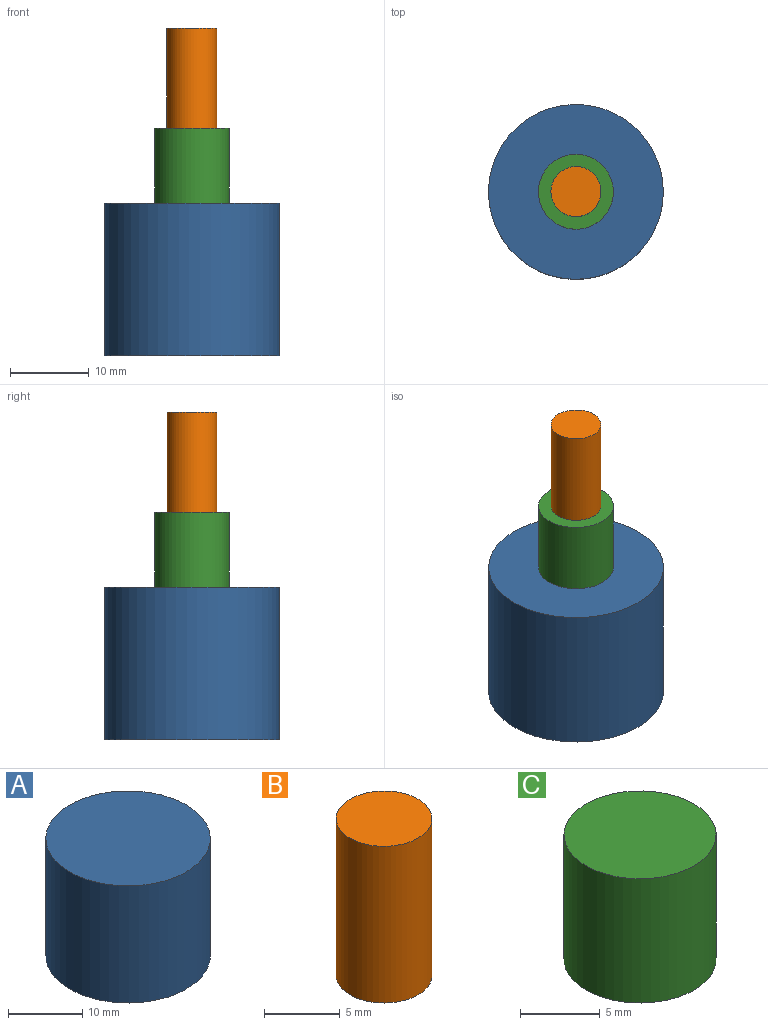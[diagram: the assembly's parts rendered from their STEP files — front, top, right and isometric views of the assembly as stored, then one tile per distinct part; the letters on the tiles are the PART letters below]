
ASSEMBLY  parts=3 mates=2
PART A: 3 faces, bbox 22.2x22.2x19.4 mm
  f0: cylinder r=11.11mm len=22.23mm, axis (0,0,-1), area 1353.2mm2, adj f1,f2
  f1: plane 22.23x22.23mm, normal (0,0,1), area 387.9mm2, adj f0
  f2: plane 22.23x22.23mm, normal (0,0,-1), area 387.9mm2, adj f0
PART B: 3 faces, bbox 6.4x6.4x12.7 mm
  f0: cylinder r=3.17mm len=12.7mm, axis (0,0,-1), area 253.4mm2, adj f1,f2
  f1: plane 6.35x6.35mm, normal (0,0,1), area 31.7mm2, adj f0
  f2: plane 6.35x6.35mm, normal (0,0,-1), area 31.7mm2, adj f0
PART C: 3 faces, bbox 9.5x9.5x9.5 mm
  f0: cylinder r=4.76mm len=9.53mm, axis (0,0,-1), area 285mm2, adj f1,f2
  f1: plane 9.53x9.53mm, normal (0,0,1), area 71.3mm2, adj f0
  f2: plane 9.53x9.53mm, normal (0,0,-1), area 71.3mm2, adj f0
PLACE A t=(-8,-0.15,-2.99)mm fixed
PLACE B rot(axis=(0,0,-1),27.9deg) t=(-8,-0.15,25.91)mm
PLACE C t=(-8,-0.15,16.39)mm
MATE revolute C.f0 <-> B.f0  axis (0,0,1) through (-8,-0.15,25.91)mm
MATE fastened A.f0 <-> C.f0  axis (0,0,1) through (-8,-0.15,16.39)mm
